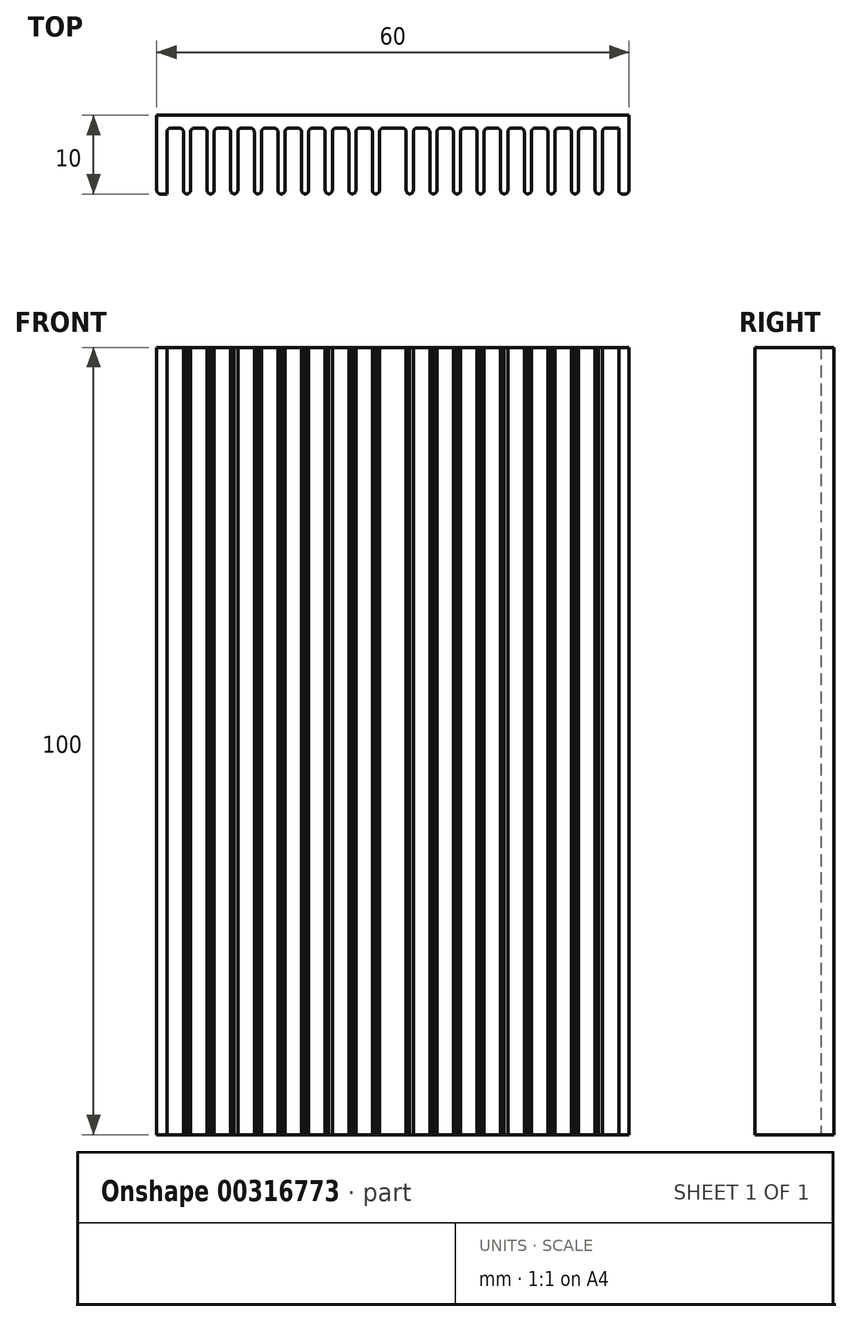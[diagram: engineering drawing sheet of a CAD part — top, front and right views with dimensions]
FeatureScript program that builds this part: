
annotation { "Feature Type Name" : "Feature", "Feature Type Description" : "" }
export const myFeature = defineFeature(function(context is Context, id is Id, definition is map)
    precondition{}
    {
        {
            var Q0;
            Q0=qCreatedBy(makeId("Front.planeOp"),FACE);
            var sketch = newSketch(context, id + "F0", { "sketchPlane" : qUnion([Q0])});
            skLineSegment(sketch, "E0.bottom", {"start": v(30, 50) * mm, "end": v(-30, 50) * mm});
            skLineSegment(sketch, "E0.top", {"start": v(30, -50) * mm, "end": v(-30, -50) * mm});
            skLineSegment(sketch, "E0.left", {"start": v(30, 50) * mm, "end": v(30, -50) * mm});
            skLineSegment(sketch, "E0.right", {"start": v(-30, 50) * mm, "end": v(-30, -50) * mm});
            skPoint(sketch, "E0.middle", {"position": v(0, 0) * mm});
            skSolve(sketch);
        }
        {
            var Q0;
            Q0=makeQuery(id+"F0.imprint","IMPRINT",FACE,{"disambiguationData":[TD([[makeQuery(id+"F0.imprint","IMPRINT",EDGE,{"derivedFrom":sQuery(id+"F0.wireOp",EDGE,"E0.bottom")}),1.0]])]});
            extrude(context, id + "F1", {"entities" : qUnion([Q0]), "depth" : 10 * mm});
        }
        {
            var Q0;
            Q0=makeQuery(id+"F1.opExtrude","SWEPT_FACE",FACE,{"disambiguationData":[OSD([sQuery(id+"F0.wireOp",EDGE,"E0.top")])]});
            var sketch = newSketch(context, id + "F2", { "sketchPlane" : qUnion([Q0])});
            skLineSegment(sketch, "E1.bottom", {"start": v(-28.7, 10) * mm, "end": v(-26.6, 10) * mm});
            skLineSegment(sketch, "E1.top", {"start": v(-28.7, 1.63) * mm, "end": v(-26.6, 1.63) * mm});
            skLineSegment(sketch, "E1.left", {"start": v(-28.7, 10) * mm, "end": v(-28.7, 1.63) * mm});
            skLineSegment(sketch, "E1.right", {"start": v(-26.6, 10) * mm, "end": v(-26.6, 1.63) * mm});
            skLineSegment(sketch, "E2.1.0.0", {"start": v(-25.7, 10) * mm, "end": v(-23.6, 10) * mm});
            skLineSegment(sketch, "E2.1.0.1", {"start": v(-25.7, 1.63) * mm, "end": v(-23.6, 1.63) * mm});
            skLineSegment(sketch, "E2.1.0.2", {"start": v(-25.7, 10) * mm, "end": v(-25.7, 1.63) * mm});
            skLineSegment(sketch, "E2.1.0.3", {"start": v(-23.6, 10) * mm, "end": v(-23.6, 1.63) * mm});
            skLineSegment(sketch, "E2.2.0.0", {"start": v(-22.7, 10) * mm, "end": v(-20.6, 10) * mm});
            skLineSegment(sketch, "E2.2.0.1", {"start": v(-22.7, 1.63) * mm, "end": v(-20.6, 1.63) * mm});
            skLineSegment(sketch, "E2.2.0.2", {"start": v(-22.7, 10) * mm, "end": v(-22.7, 1.63) * mm});
            skLineSegment(sketch, "E2.2.0.3", {"start": v(-20.6, 10) * mm, "end": v(-20.6, 1.63) * mm});
            skLineSegment(sketch, "E2.3.0.0", {"start": v(-19.7, 10) * mm, "end": v(-17.6, 10) * mm});
            skLineSegment(sketch, "E2.3.0.1", {"start": v(-19.7, 1.63) * mm, "end": v(-17.6, 1.63) * mm});
            skLineSegment(sketch, "E2.3.0.2", {"start": v(-19.7, 10) * mm, "end": v(-19.7, 1.63) * mm});
            skLineSegment(sketch, "E2.3.0.3", {"start": v(-17.6, 10) * mm, "end": v(-17.6, 1.63) * mm});
            skLineSegment(sketch, "E2.4.0.0", {"start": v(-16.7, 10) * mm, "end": v(-14.6, 10) * mm});
            skLineSegment(sketch, "E2.4.0.1", {"start": v(-16.7, 1.63) * mm, "end": v(-14.6, 1.63) * mm});
            skLineSegment(sketch, "E2.4.0.2", {"start": v(-16.7, 10) * mm, "end": v(-16.7, 1.63) * mm});
            skLineSegment(sketch, "E2.4.0.3", {"start": v(-14.6, 10) * mm, "end": v(-14.6, 1.63) * mm});
            skLineSegment(sketch, "E2.5.0.0", {"start": v(-13.7, 10) * mm, "end": v(-11.6, 10) * mm});
            skLineSegment(sketch, "E2.5.0.1", {"start": v(-13.7, 1.63) * mm, "end": v(-11.6, 1.63) * mm});
            skLineSegment(sketch, "E2.5.0.2", {"start": v(-13.7, 10) * mm, "end": v(-13.7, 1.63) * mm});
            skLineSegment(sketch, "E2.5.0.3", {"start": v(-11.6, 10) * mm, "end": v(-11.6, 1.63) * mm});
            skLineSegment(sketch, "E2.6.0.0", {"start": v(-10.7, 10) * mm, "end": v(-8.6, 10) * mm});
            skLineSegment(sketch, "E2.6.0.1", {"start": v(-10.7, 1.63) * mm, "end": v(-8.6, 1.63) * mm});
            skLineSegment(sketch, "E2.6.0.2", {"start": v(-10.7, 10) * mm, "end": v(-10.7, 1.63) * mm});
            skLineSegment(sketch, "E2.6.0.3", {"start": v(-8.6, 10) * mm, "end": v(-8.6, 1.63) * mm});
            skLineSegment(sketch, "E2.7.0.0", {"start": v(-7.7, 10) * mm, "end": v(-5.6, 10) * mm});
            skLineSegment(sketch, "E2.7.0.1", {"start": v(-7.7, 1.63) * mm, "end": v(-5.6, 1.63) * mm});
            skLineSegment(sketch, "E2.7.0.2", {"start": v(-7.7, 10) * mm, "end": v(-7.7, 1.63) * mm});
            skLineSegment(sketch, "E2.7.0.3", {"start": v(-5.6, 10) * mm, "end": v(-5.6, 1.63) * mm});
            skLineSegment(sketch, "E2.8.0.0", {"start": v(-4.7, 10) * mm, "end": v(-2.6, 10) * mm});
            skLineSegment(sketch, "E2.8.0.1", {"start": v(-4.7, 1.63) * mm, "end": v(-2.6, 1.63) * mm});
            skLineSegment(sketch, "E2.8.0.2", {"start": v(-4.7, 10) * mm, "end": v(-4.7, 1.63) * mm});
            skLineSegment(sketch, "E2.8.0.3", {"start": v(-2.6, 10) * mm, "end": v(-2.6, 1.63) * mm});
            skLineSegment(sketch, "E2.9.0.0", {"start": v(-1.7, 10) * mm, "end": v(0.4, 10) * mm});
            skLineSegment(sketch, "E2.9.0.1", {"start": v(-1.7, 1.63) * mm, "end": v(0.4, 1.63) * mm});
            skLineSegment(sketch, "E2.9.0.2", {"start": v(-1.7, 10) * mm, "end": v(-1.7, 1.63) * mm});
            skLineSegment(sketch, "E2.9.0.3", {"start": v(0.4, 10) * mm, "end": v(0.4, 1.63) * mm});
            skLineSegment(sketch, "E2.direction1", {"start": v(-28.7, 1.63) * mm, "end": v(-25.7, 1.63) * mm, "construction": true});
            skLineSegment(sketch, "E3.MirrorCS", {"start": v(25.7, 1.63) * mm, "end": v(23.6, 1.63) * mm});
            skLineSegment(sketch, "E4.MirrorCS", {"start": v(22.7, 1.63) * mm, "end": v(20.6, 1.63) * mm});
            skLineSegment(sketch, "E5.MirrorCS", {"start": v(19.7, 10) * mm, "end": v(17.6, 10) * mm});
            skLineSegment(sketch, "E6.MirrorCS", {"start": v(7.7, 1.63) * mm, "end": v(5.6, 1.63) * mm});
            skLineSegment(sketch, "E7.MirrorCS", {"start": v(19.7, 1.63) * mm, "end": v(17.6, 1.63) * mm});
            skLineSegment(sketch, "E8.MirrorCS", {"start": v(28.7, 1.63) * mm, "end": v(26.6, 1.63) * mm});
            skLineSegment(sketch, "E9.MirrorCS", {"start": v(10.7, 10) * mm, "end": v(8.6, 10) * mm});
            skLineSegment(sketch, "E10.MirrorCS", {"start": v(28.7, 1.63) * mm, "end": v(25.7, 1.63) * mm, "construction": true});
            skLineSegment(sketch, "E11.MirrorCS", {"start": v(4.7, 10) * mm, "end": v(2.6, 10) * mm});
            skLineSegment(sketch, "E12.MirrorCS", {"start": v(22.7, 10) * mm, "end": v(20.6, 10) * mm});
            skLineSegment(sketch, "E13.MirrorCS", {"start": v(10.7, 1.63) * mm, "end": v(8.6, 1.63) * mm});
            skLineSegment(sketch, "E14.MirrorCS", {"start": v(13.7, 10) * mm, "end": v(11.6, 10) * mm});
            skLineSegment(sketch, "E15.MirrorCS", {"start": v(1.7, 10) * mm, "end": v(-0.4, 10) * mm});
            skLineSegment(sketch, "E16.MirrorCS", {"start": v(16.7, 1.63) * mm, "end": v(14.6, 1.63) * mm});
            skLineSegment(sketch, "E17.MirrorCS", {"start": v(4.7, 1.63) * mm, "end": v(2.6, 1.63) * mm});
            skLineSegment(sketch, "E18.MirrorCS", {"start": v(16.7, 10) * mm, "end": v(14.6, 10) * mm});
            skLineSegment(sketch, "E19.MirrorCS", {"start": v(25.7, 10) * mm, "end": v(23.6, 10) * mm});
            skLineSegment(sketch, "E20.MirrorCS", {"start": v(7.7, 10) * mm, "end": v(5.6, 10) * mm});
            skLineSegment(sketch, "E21.MirrorCS", {"start": v(1.7, 1.63) * mm, "end": v(-0.4, 1.63) * mm});
            skLineSegment(sketch, "E22.MirrorCS", {"start": v(28.7, 10) * mm, "end": v(26.6, 10) * mm});
            skLineSegment(sketch, "E23.MirrorCS", {"start": v(13.7, 1.63) * mm, "end": v(11.6, 1.63) * mm});
            skLineSegment(sketch, "E24.MirrorCS", {"start": v(25.7, 10) * mm, "end": v(25.7, 1.63) * mm});
            skLineSegment(sketch, "E25.MirrorCS", {"start": v(23.6, 10) * mm, "end": v(23.6, 1.63) * mm});
            skLineSegment(sketch, "E26.MirrorCS", {"start": v(-0.4, 10) * mm, "end": v(-0.4, 1.63) * mm});
            skLineSegment(sketch, "E27.MirrorCS", {"start": v(13.7, 10) * mm, "end": v(13.7, 1.63) * mm});
            skLineSegment(sketch, "E28.MirrorCS", {"start": v(5.6, 10) * mm, "end": v(5.6, 1.63) * mm});
            skLineSegment(sketch, "E29.MirrorCS", {"start": v(22.7, 10) * mm, "end": v(22.7, 1.63) * mm});
            skLineSegment(sketch, "E30.MirrorCS", {"start": v(20.6, 10) * mm, "end": v(20.6, 1.63) * mm});
            skLineSegment(sketch, "E31.MirrorCS", {"start": v(7.7, 10) * mm, "end": v(7.7, 1.63) * mm});
            skLineSegment(sketch, "E32.MirrorCS", {"start": v(4.7, 10) * mm, "end": v(4.7, 1.63) * mm});
            skLineSegment(sketch, "E33.MirrorCS", {"start": v(16.7, 10) * mm, "end": v(16.7, 1.63) * mm});
            skLineSegment(sketch, "E34.MirrorCS", {"start": v(10.7, 10) * mm, "end": v(10.7, 1.63) * mm});
            skLineSegment(sketch, "E35.MirrorCS", {"start": v(8.6, 10) * mm, "end": v(8.6, 1.63) * mm});
            skLineSegment(sketch, "E36.MirrorCS", {"start": v(19.7, 10) * mm, "end": v(19.7, 1.63) * mm});
            skLineSegment(sketch, "E37.MirrorCS", {"start": v(26.6, 10) * mm, "end": v(26.6, 1.63) * mm});
            skLineSegment(sketch, "E38.MirrorCS", {"start": v(28.7, 10) * mm, "end": v(28.7, 1.63) * mm});
            skLineSegment(sketch, "E39.MirrorCS", {"start": v(1.7, 10) * mm, "end": v(1.7, 1.63) * mm});
            skLineSegment(sketch, "E40.MirrorCS", {"start": v(2.6, 10) * mm, "end": v(2.6, 1.63) * mm});
            skLineSegment(sketch, "E41.MirrorCS", {"start": v(17.6, 10) * mm, "end": v(17.6, 1.63) * mm});
            skLineSegment(sketch, "E42.MirrorCS", {"start": v(11.6, 10) * mm, "end": v(11.6, 1.63) * mm});
            skLineSegment(sketch, "E43.MirrorCS", {"start": v(14.6, 10) * mm, "end": v(14.6, 1.63) * mm});
            skSolve(sketch);
        }
        {
            var Q0;
            Q0=makeQuery(id+"F2.imprint","IMPRINT",FACE,{"disambiguationData":[TD([[makeQuery(id+"F2.imprint","IMPRINT",EDGE,{"derivedFrom":sQuery(id+"F2.wireOp",EDGE,"E2.1.0.0")}),1.0]])]});
            var Q1;
            Q1=makeQuery(id+"F2.imprint","IMPRINT",FACE,{"disambiguationData":[TD([[makeQuery(id+"F2.imprint","IMPRINT",EDGE,{"derivedFrom":sQuery(id+"F2.wireOp",EDGE,"E2.2.0.0")}),1.0]])]});
            var Q2;
            Q2=makeQuery(id+"F2.imprint","IMPRINT",FACE,{"disambiguationData":[TD([[makeQuery(id+"F2.imprint","IMPRINT",EDGE,{"derivedFrom":sQuery(id+"F2.wireOp",EDGE,"E2.3.0.0")}),1.0]])]});
            var Q3;
            Q3=makeQuery(id+"F2.imprint","IMPRINT",FACE,{"disambiguationData":[TD([[makeQuery(id+"F2.imprint","IMPRINT",EDGE,{"derivedFrom":sQuery(id+"F2.wireOp",EDGE,"E2.4.0.0")}),1.0]])]});
            var Q4;
            Q4=makeQuery(id+"F2.imprint","IMPRINT",FACE,{"disambiguationData":[TD([[makeQuery(id+"F2.imprint","IMPRINT",EDGE,{"derivedFrom":sQuery(id+"F2.wireOp",EDGE,"E2.5.0.0")}),1.0]])]});
            var Q5;
            Q5=makeQuery(id+"F2.imprint","IMPRINT",FACE,{"disambiguationData":[TD([[makeQuery(id+"F2.imprint","IMPRINT",EDGE,{"derivedFrom":sQuery(id+"F2.wireOp",EDGE,"E2.6.0.0")}),1.0]])]});
            var Q6;
            Q6=makeQuery(id+"F2.imprint","IMPRINT",FACE,{"disambiguationData":[TD([[makeQuery(id+"F2.imprint","IMPRINT",EDGE,{"derivedFrom":sQuery(id+"F2.wireOp",EDGE,"E2.7.0.0")}),1.0]])]});
            var Q7;
            Q7=makeQuery(id+"F2.imprint","IMPRINT",FACE,{"disambiguationData":[TD([[makeQuery(id+"F2.imprint","IMPRINT",EDGE,{"derivedFrom":sQuery(id+"F2.wireOp",EDGE,"E2.8.0.0")}),1.0]])]});
            var Q8;
            Q8=makeQuery(id+"F2.imprint","IMPRINT",FACE,{"disambiguationData":[TD([[makeQuery(id+"F2.imprint","IMPRINT",EDGE,{"derivedFrom":sQuery(id+"F2.wireOp",EDGE,"E2.9.0.0")}),1.0]])]});
            var Q9;
            Q9=makeQuery(id+"F2.imprint","IMPRINT",FACE,{"disambiguationData":[TD([[makeQuery(id+"F2.imprint","IMPRINT",EDGE,{"derivedFrom":sQuery(id+"F2.wireOp",EDGE,"E3.MirrorCS")}),-1.0]])]});
            var Q10;
            Q10=makeQuery(id+"F2.imprint","IMPRINT",FACE,{"disambiguationData":[TD([[makeQuery(id+"F2.imprint","IMPRINT",EDGE,{"derivedFrom":sQuery(id+"F2.wireOp",EDGE,"E4.MirrorCS")}),-1.0]])]});
            var Q11;
            Q11=makeQuery(id+"F2.imprint","IMPRINT",FACE,{"disambiguationData":[TD([[makeQuery(id+"F2.imprint","IMPRINT",EDGE,{"derivedFrom":sQuery(id+"F2.wireOp",EDGE,"E5.MirrorCS")}),1.0]])]});
            var Q12;
            Q12=makeQuery(id+"F2.imprint","IMPRINT",FACE,{"disambiguationData":[TD([[makeQuery(id+"F2.imprint","IMPRINT",EDGE,{"derivedFrom":sQuery(id+"F2.wireOp",EDGE,"E6.MirrorCS")}),-1.0]])]});
            var Q13;
            Q13=makeQuery(id+"F2.imprint","IMPRINT",FACE,{"disambiguationData":[TD([[makeQuery(id+"F2.imprint","IMPRINT",EDGE,{"derivedFrom":sQuery(id+"F2.wireOp",EDGE,"E8.MirrorCS")}),-1.0]])]});
            var Q14;
            Q14=makeQuery(id+"F2.imprint","IMPRINT",FACE,{"disambiguationData":[TD([[makeQuery(id+"F2.imprint","IMPRINT",EDGE,{"derivedFrom":sQuery(id+"F2.wireOp",EDGE,"E9.MirrorCS")}),1.0]])]});
            var Q15;
            Q15=makeQuery(id+"F2.imprint","IMPRINT",FACE,{"disambiguationData":[TD([[makeQuery(id+"F2.imprint","IMPRINT",EDGE,{"derivedFrom":sQuery(id+"F2.wireOp",EDGE,"E11.MirrorCS")}),1.0]])]});
            var Q16;
            Q16=makeQuery(id+"F2.imprint","IMPRINT",FACE,{"disambiguationData":[TD([[makeQuery(id+"F2.imprint","IMPRINT",EDGE,{"derivedFrom":sQuery(id+"F2.wireOp",EDGE,"E14.MirrorCS")}),1.0]])]});
            var Q17;
            Q17=makeQuery(id+"F2.imprint","IMPRINT",FACE,{"disambiguationData":[TD([[makeQuery(id+"F2.imprint","IMPRINT",EDGE,{"derivedFrom":sQuery(id+"F2.wireOp",EDGE,"E15.MirrorCS")}),1.0]])]});
            var Q18;
            Q18=makeQuery(id+"F2.imprint","IMPRINT",FACE,{"disambiguationData":[TD([[makeQuery(id+"F2.imprint","IMPRINT",EDGE,{"derivedFrom":sQuery(id+"F2.wireOp",EDGE,"E16.MirrorCS")}),-1.0]])]});
            var Q19;
            Q19=makeQuery(id+"F2.imprint","IMPRINT",FACE,{"disambiguationData":[TD([[makeQuery(id+"F2.imprint","IMPRINT",EDGE,{"derivedFrom":sQuery(id+"F2.wireOp",EDGE,"E1.bottom")}),1.0]])]});
            extrude(context, id + "F3", {"entities" : qUnion([Q0, Q1, Q2, Q3, Q4, Q5, Q6, Q7, Q8, Q9, Q10, Q11, Q12, Q13, Q14, Q15, Q16, Q17, Q18, Q19]), "operationType" : NewBodyOperationType.REMOVE, "endBound" : BoundingType.THROUGH_ALL, "oppositeDirection" : true, "depth" : 25 * mm});
        }
        {
            var Q0;
            Q0=makeQuery(id+"F3.boolean.opBoolean","COPY",EDGE,{"derivedFrom":makeQuery(id+"F3.opExtrude","SWEPT_EDGE",EDGE,{"disambiguationData":[OSD([sQuery(id+"F0.wireOp",EDGE,"E0.top"),sQuery(id+"F2.wireOp",EDGE,"E1.bottom"),sQuery(id+"F2.wireOp",EDGE,"E1.left")])]})});
            var Q1;
            Q1=makeQuery(id+"F3.boolean.opBoolean","COPY",EDGE,{"derivedFrom":makeQuery(id+"F3.opExtrude","SWEPT_EDGE",EDGE,{"disambiguationData":[OSD([sQuery(id+"F2.wireOp",EDGE,"E1.top"),sQuery(id+"F2.wireOp",EDGE,"E1.left")])]})});
            var Q2;
            Q2=makeQuery(id+"F3.boolean.opBoolean","COPY",EDGE,{"derivedFrom":makeQuery(id+"F3.opExtrude","SWEPT_EDGE",EDGE,{"disambiguationData":[OSD([sQuery(id+"F2.wireOp",EDGE,"E1.top"),sQuery(id+"F2.wireOp",EDGE,"E1.right")])]})});
            var Q3;
            Q3=makeQuery(id+"F3.boolean.opBoolean","COPY",EDGE,{"derivedFrom":makeQuery(id+"F3.opExtrude","SWEPT_EDGE",EDGE,{"disambiguationData":[OSD([sQuery(id+"F0.wireOp",EDGE,"E0.top"),sQuery(id+"F2.wireOp",EDGE,"E1.bottom"),sQuery(id+"F2.wireOp",EDGE,"E1.right")])]})});
            var Q4;
            Q4=makeQuery(id+"F3.boolean.opBoolean","COPY",EDGE,{"derivedFrom":makeQuery(id+"F3.opExtrude","SWEPT_EDGE",EDGE,{"disambiguationData":[OSD([sQuery(id+"F0.wireOp",EDGE,"E0.top"),sQuery(id+"F2.wireOp",EDGE,"E2.1.0.0"),sQuery(id+"F2.wireOp",EDGE,"E2.1.0.2")])]})});
            var Q5;
            Q5=makeQuery(id+"F3.boolean.opBoolean","COPY",EDGE,{"derivedFrom":makeQuery(id+"F3.opExtrude","SWEPT_EDGE",EDGE,{"disambiguationData":[OSD([sQuery(id+"F2.wireOp",EDGE,"E2.1.0.1"),sQuery(id+"F2.wireOp",EDGE,"E2.1.0.2")])]})});
            var Q6;
            Q6=makeQuery(id+"F3.boolean.opBoolean","COPY",EDGE,{"derivedFrom":makeQuery(id+"F3.opExtrude","SWEPT_EDGE",EDGE,{"disambiguationData":[OSD([sQuery(id+"F2.wireOp",EDGE,"E2.2.0.1"),sQuery(id+"F2.wireOp",EDGE,"E2.2.0.2")])]})});
            var Q7;
            Q7=makeQuery(id+"F3.boolean.opBoolean","COPY",EDGE,{"derivedFrom":makeQuery(id+"F3.opExtrude","SWEPT_EDGE",EDGE,{"disambiguationData":[OSD([sQuery(id+"F2.wireOp",EDGE,"E2.3.0.1"),sQuery(id+"F2.wireOp",EDGE,"E2.3.0.2")])]})});
            var Q8;
            Q8=makeQuery(id+"F3.boolean.opBoolean","COPY",EDGE,{"derivedFrom":makeQuery(id+"F3.opExtrude","SWEPT_EDGE",EDGE,{"disambiguationData":[OSD([sQuery(id+"F2.wireOp",EDGE,"E2.4.0.1"),sQuery(id+"F2.wireOp",EDGE,"E2.4.0.2")])]})});
            var Q9;
            Q9=makeQuery(id+"F3.boolean.opBoolean","COPY",EDGE,{"derivedFrom":makeQuery(id+"F3.opExtrude","SWEPT_EDGE",EDGE,{"disambiguationData":[OSD([sQuery(id+"F2.wireOp",EDGE,"E2.5.0.1"),sQuery(id+"F2.wireOp",EDGE,"E2.5.0.2")])]})});
            var Q10;
            Q10=makeQuery(id+"F3.boolean.opBoolean","COPY",EDGE,{"derivedFrom":makeQuery(id+"F3.opExtrude","SWEPT_EDGE",EDGE,{"disambiguationData":[OSD([sQuery(id+"F2.wireOp",EDGE,"E2.6.0.1"),sQuery(id+"F2.wireOp",EDGE,"E2.6.0.2")])]})});
            var Q11;
            Q11=makeQuery(id+"F3.boolean.opBoolean","COPY",EDGE,{"derivedFrom":makeQuery(id+"F3.opExtrude","SWEPT_EDGE",EDGE,{"disambiguationData":[OSD([sQuery(id+"F2.wireOp",EDGE,"E2.7.0.1"),sQuery(id+"F2.wireOp",EDGE,"E2.7.0.2")])]})});
            var Q12;
            Q12=makeQuery(id+"F3.boolean.opBoolean","COPY",EDGE,{"derivedFrom":makeQuery(id+"F3.opExtrude","SWEPT_EDGE",EDGE,{"disambiguationData":[OSD([sQuery(id+"F2.wireOp",EDGE,"E2.8.0.1"),sQuery(id+"F2.wireOp",EDGE,"E2.8.0.2")])]})});
            var Q13;
            Q13=makeQuery(id+"F3.boolean.opBoolean","COPY",EDGE,{"derivedFrom":makeQuery(id+"F3.opExtrude","SWEPT_EDGE",EDGE,{"disambiguationData":[OSD([sQuery(id+"F2.wireOp",EDGE,"E2.9.0.1"),sQuery(id+"F2.wireOp",EDGE,"E2.9.0.2")])]})});
            var Q14;
            Q14=makeQuery(id+"F3.boolean.opBoolean","COPY",EDGE,{"derivedFrom":makeQuery(id+"F3.opExtrude","SWEPT_EDGE",EDGE,{"disambiguationData":[OSD([sQuery(id+"F2.wireOp",EDGE,"E17.MirrorCS"),sQuery(id+"F2.wireOp",EDGE,"E40.MirrorCS")])]})});
            var Q15;
            Q15=makeQuery(id+"F3.boolean.opBoolean","COPY",EDGE,{"derivedFrom":makeQuery(id+"F3.opExtrude","SWEPT_EDGE",EDGE,{"disambiguationData":[OSD([sQuery(id+"F2.wireOp",EDGE,"E6.MirrorCS"),sQuery(id+"F2.wireOp",EDGE,"E28.MirrorCS")])]})});
            var Q16;
            Q16=makeQuery(id+"F3.boolean.opBoolean","COPY",EDGE,{"derivedFrom":makeQuery(id+"F3.opExtrude","SWEPT_EDGE",EDGE,{"disambiguationData":[OSD([sQuery(id+"F2.wireOp",EDGE,"E13.MirrorCS"),sQuery(id+"F2.wireOp",EDGE,"E35.MirrorCS")])]})});
            var Q17;
            Q17=makeQuery(id+"F3.boolean.opBoolean","COPY",EDGE,{"derivedFrom":makeQuery(id+"F3.opExtrude","SWEPT_EDGE",EDGE,{"disambiguationData":[OSD([sQuery(id+"F2.wireOp",EDGE,"E23.MirrorCS"),sQuery(id+"F2.wireOp",EDGE,"E42.MirrorCS")])]})});
            var Q18;
            Q18=makeQuery(id+"F3.boolean.opBoolean","COPY",EDGE,{"derivedFrom":makeQuery(id+"F3.opExtrude","SWEPT_EDGE",EDGE,{"disambiguationData":[OSD([sQuery(id+"F2.wireOp",EDGE,"E16.MirrorCS"),sQuery(id+"F2.wireOp",EDGE,"E43.MirrorCS")])]})});
            var Q19;
            Q19=makeQuery(id+"F3.boolean.opBoolean","COPY",EDGE,{"derivedFrom":makeQuery(id+"F3.opExtrude","SWEPT_EDGE",EDGE,{"disambiguationData":[OSD([sQuery(id+"F2.wireOp",EDGE,"E7.MirrorCS"),sQuery(id+"F2.wireOp",EDGE,"E41.MirrorCS")])]})});
            var Q20;
            Q20=makeQuery(id+"F3.boolean.opBoolean","COPY",EDGE,{"derivedFrom":makeQuery(id+"F3.opExtrude","SWEPT_EDGE",EDGE,{"disambiguationData":[OSD([sQuery(id+"F2.wireOp",EDGE,"E4.MirrorCS"),sQuery(id+"F2.wireOp",EDGE,"E30.MirrorCS")])]})});
            var Q21;
            Q21=makeQuery(id+"F3.boolean.opBoolean","COPY",EDGE,{"derivedFrom":makeQuery(id+"F3.opExtrude","SWEPT_EDGE",EDGE,{"disambiguationData":[OSD([sQuery(id+"F2.wireOp",EDGE,"E3.MirrorCS"),sQuery(id+"F2.wireOp",EDGE,"E25.MirrorCS")])]})});
            var Q22;
            Q22=makeQuery(id+"F3.boolean.opBoolean","COPY",EDGE,{"derivedFrom":makeQuery(id+"F3.opExtrude","SWEPT_EDGE",EDGE,{"disambiguationData":[OSD([sQuery(id+"F2.wireOp",EDGE,"E8.MirrorCS"),sQuery(id+"F2.wireOp",EDGE,"E37.MirrorCS")])]})});
            var Q23;
            Q23=makeQuery(id+"F3.boolean.opBoolean","COPY",EDGE,{"derivedFrom":makeQuery(id+"F3.opExtrude","SWEPT_EDGE",EDGE,{"disambiguationData":[OSD([sQuery(id+"F0.wireOp",EDGE,"E0.top"),sQuery(id+"F2.wireOp",EDGE,"E2.2.0.0"),sQuery(id+"F2.wireOp",EDGE,"E2.2.0.2")])]})});
            var Q24;
            Q24=makeQuery(id+"F3.boolean.opBoolean","COPY",EDGE,{"derivedFrom":makeQuery(id+"F3.opExtrude","SWEPT_EDGE",EDGE,{"disambiguationData":[OSD([sQuery(id+"F0.wireOp",EDGE,"E0.top"),sQuery(id+"F2.wireOp",EDGE,"E2.3.0.0"),sQuery(id+"F2.wireOp",EDGE,"E2.3.0.2")])]})});
            var Q25;
            Q25=makeQuery(id+"F3.boolean.opBoolean","COPY",EDGE,{"derivedFrom":makeQuery(id+"F3.opExtrude","SWEPT_EDGE",EDGE,{"disambiguationData":[OSD([sQuery(id+"F0.wireOp",EDGE,"E0.top"),sQuery(id+"F2.wireOp",EDGE,"E2.4.0.0"),sQuery(id+"F2.wireOp",EDGE,"E2.4.0.2")])]})});
            var Q26;
            Q26=makeQuery(id+"F3.boolean.opBoolean","COPY",EDGE,{"derivedFrom":makeQuery(id+"F3.opExtrude","SWEPT_EDGE",EDGE,{"disambiguationData":[OSD([sQuery(id+"F0.wireOp",EDGE,"E0.top"),sQuery(id+"F2.wireOp",EDGE,"E2.5.0.0"),sQuery(id+"F2.wireOp",EDGE,"E2.5.0.2")])]})});
            var Q27;
            Q27=makeQuery(id+"F3.boolean.opBoolean","COPY",EDGE,{"derivedFrom":makeQuery(id+"F3.opExtrude","SWEPT_EDGE",EDGE,{"disambiguationData":[OSD([sQuery(id+"F0.wireOp",EDGE,"E0.top"),sQuery(id+"F2.wireOp",EDGE,"E2.6.0.0"),sQuery(id+"F2.wireOp",EDGE,"E2.6.0.2")])]})});
            var Q28;
            Q28=makeQuery(id+"F3.boolean.opBoolean","COPY",EDGE,{"derivedFrom":makeQuery(id+"F3.opExtrude","SWEPT_EDGE",EDGE,{"disambiguationData":[OSD([sQuery(id+"F0.wireOp",EDGE,"E0.top"),sQuery(id+"F2.wireOp",EDGE,"E2.7.0.0"),sQuery(id+"F2.wireOp",EDGE,"E2.7.0.2")])]})});
            var Q29;
            Q29=makeQuery(id+"F3.boolean.opBoolean","COPY",EDGE,{"derivedFrom":makeQuery(id+"F3.opExtrude","SWEPT_EDGE",EDGE,{"disambiguationData":[OSD([sQuery(id+"F0.wireOp",EDGE,"E0.top"),sQuery(id+"F2.wireOp",EDGE,"E2.8.0.0"),sQuery(id+"F2.wireOp",EDGE,"E2.8.0.2")])]})});
            var Q30;
            Q30=makeQuery(id+"F3.boolean.opBoolean","COPY",EDGE,{"derivedFrom":makeQuery(id+"F3.opExtrude","SWEPT_EDGE",EDGE,{"disambiguationData":[OSD([sQuery(id+"F0.wireOp",EDGE,"E0.top"),sQuery(id+"F2.wireOp",EDGE,"E2.9.0.0"),sQuery(id+"F2.wireOp",EDGE,"E2.9.0.2")])]})});
            var Q31;
            Q31=makeQuery(id+"F3.boolean.opBoolean","COPY",EDGE,{"derivedFrom":makeQuery(id+"F3.opExtrude","SWEPT_EDGE",EDGE,{"disambiguationData":[OSD([sQuery(id+"F0.wireOp",EDGE,"E0.top"),sQuery(id+"F2.wireOp",EDGE,"E11.MirrorCS"),sQuery(id+"F2.wireOp",EDGE,"E40.MirrorCS")])]})});
            var Q32;
            Q32=makeQuery(id+"F3.boolean.opBoolean","COPY",EDGE,{"derivedFrom":makeQuery(id+"F3.opExtrude","SWEPT_EDGE",EDGE,{"disambiguationData":[OSD([sQuery(id+"F0.wireOp",EDGE,"E0.top"),sQuery(id+"F2.wireOp",EDGE,"E20.MirrorCS"),sQuery(id+"F2.wireOp",EDGE,"E28.MirrorCS")])]})});
            var Q33;
            Q33=makeQuery(id+"F3.boolean.opBoolean","COPY",EDGE,{"derivedFrom":makeQuery(id+"F3.opExtrude","SWEPT_EDGE",EDGE,{"disambiguationData":[OSD([sQuery(id+"F0.wireOp",EDGE,"E0.top"),sQuery(id+"F2.wireOp",EDGE,"E9.MirrorCS"),sQuery(id+"F2.wireOp",EDGE,"E35.MirrorCS")])]})});
            var Q34;
            Q34=makeQuery(id+"F3.boolean.opBoolean","COPY",EDGE,{"derivedFrom":makeQuery(id+"F3.opExtrude","SWEPT_EDGE",EDGE,{"disambiguationData":[OSD([sQuery(id+"F0.wireOp",EDGE,"E0.top"),sQuery(id+"F2.wireOp",EDGE,"E14.MirrorCS"),sQuery(id+"F2.wireOp",EDGE,"E42.MirrorCS")])]})});
            var Q35;
            Q35=makeQuery(id+"F3.boolean.opBoolean","COPY",EDGE,{"derivedFrom":makeQuery(id+"F3.opExtrude","SWEPT_EDGE",EDGE,{"disambiguationData":[OSD([sQuery(id+"F0.wireOp",EDGE,"E0.top"),sQuery(id+"F2.wireOp",EDGE,"E18.MirrorCS"),sQuery(id+"F2.wireOp",EDGE,"E43.MirrorCS")])]})});
            var Q36;
            Q36=makeQuery(id+"F3.boolean.opBoolean","COPY",EDGE,{"derivedFrom":makeQuery(id+"F3.opExtrude","SWEPT_EDGE",EDGE,{"disambiguationData":[OSD([sQuery(id+"F0.wireOp",EDGE,"E0.top"),sQuery(id+"F2.wireOp",EDGE,"E5.MirrorCS"),sQuery(id+"F2.wireOp",EDGE,"E41.MirrorCS")])]})});
            var Q37;
            Q37=makeQuery(id+"F3.boolean.opBoolean","COPY",EDGE,{"derivedFrom":makeQuery(id+"F3.opExtrude","SWEPT_EDGE",EDGE,{"disambiguationData":[OSD([sQuery(id+"F0.wireOp",EDGE,"E0.top"),sQuery(id+"F2.wireOp",EDGE,"E12.MirrorCS"),sQuery(id+"F2.wireOp",EDGE,"E30.MirrorCS")])]})});
            var Q38;
            Q38=makeQuery(id+"F3.boolean.opBoolean","COPY",EDGE,{"derivedFrom":makeQuery(id+"F3.opExtrude","SWEPT_EDGE",EDGE,{"disambiguationData":[OSD([sQuery(id+"F0.wireOp",EDGE,"E0.top"),sQuery(id+"F2.wireOp",EDGE,"E19.MirrorCS"),sQuery(id+"F2.wireOp",EDGE,"E25.MirrorCS")])]})});
            var Q39;
            Q39=makeQuery(id+"F3.boolean.opBoolean","COPY",EDGE,{"derivedFrom":makeQuery(id+"F3.opExtrude","SWEPT_EDGE",EDGE,{"disambiguationData":[OSD([sQuery(id+"F0.wireOp",EDGE,"E0.top"),sQuery(id+"F2.wireOp",EDGE,"E22.MirrorCS"),sQuery(id+"F2.wireOp",EDGE,"E37.MirrorCS")])]})});
            var Q40;
            Q40=makeQuery(id+"F3.boolean.opBoolean","COPY",EDGE,{"derivedFrom":makeQuery(id+"F3.opExtrude","SWEPT_EDGE",EDGE,{"disambiguationData":[OSD([sQuery(id+"F0.wireOp",EDGE,"E0.top"),sQuery(id+"F2.wireOp",EDGE,"E22.MirrorCS"),sQuery(id+"F2.wireOp",EDGE,"E38.MirrorCS")])]})});
            var Q41;
            Q41=makeQuery(id+"F1.opExtrude","CAP_EDGE",EDGE,{"disambiguationData":[OSD([sQuery(id+"F0.wireOp",EDGE,"E0.left")])],"isStart":false});
            var Q42;
            Q42=makeQuery(id+"F1.opExtrude","CAP_EDGE",EDGE,{"disambiguationData":[OSD([sQuery(id+"F0.wireOp",EDGE,"E0.right")])],"isStart":false});
            var Q43;
            Q43=makeQuery(id+"F3.boolean.opBoolean","COPY",EDGE,{"derivedFrom":makeQuery(id+"F3.opExtrude","SWEPT_EDGE",EDGE,{"disambiguationData":[OSD([sQuery(id+"F2.wireOp",EDGE,"E2.1.0.1"),sQuery(id+"F2.wireOp",EDGE,"E2.1.0.3")])]})});
            var Q44;
            Q44=makeQuery(id+"F3.boolean.opBoolean","COPY",EDGE,{"derivedFrom":makeQuery(id+"F3.opExtrude","SWEPT_EDGE",EDGE,{"disambiguationData":[OSD([sQuery(id+"F2.wireOp",EDGE,"E2.2.0.1"),sQuery(id+"F2.wireOp",EDGE,"E2.2.0.3")])]})});
            var Q45;
            Q45=makeQuery(id+"F3.boolean.opBoolean","COPY",EDGE,{"derivedFrom":makeQuery(id+"F3.opExtrude","SWEPT_EDGE",EDGE,{"disambiguationData":[OSD([sQuery(id+"F2.wireOp",EDGE,"E2.3.0.1"),sQuery(id+"F2.wireOp",EDGE,"E2.3.0.3")])]})});
            var Q46;
            Q46=makeQuery(id+"F3.boolean.opBoolean","COPY",EDGE,{"derivedFrom":makeQuery(id+"F3.opExtrude","SWEPT_EDGE",EDGE,{"disambiguationData":[OSD([sQuery(id+"F2.wireOp",EDGE,"E2.4.0.1"),sQuery(id+"F2.wireOp",EDGE,"E2.4.0.3")])]})});
            var Q47;
            Q47=makeQuery(id+"F3.boolean.opBoolean","COPY",EDGE,{"derivedFrom":makeQuery(id+"F3.opExtrude","SWEPT_EDGE",EDGE,{"disambiguationData":[OSD([sQuery(id+"F2.wireOp",EDGE,"E2.5.0.1"),sQuery(id+"F2.wireOp",EDGE,"E2.5.0.3")])]})});
            var Q48;
            Q48=makeQuery(id+"F3.boolean.opBoolean","COPY",EDGE,{"derivedFrom":makeQuery(id+"F3.opExtrude","SWEPT_EDGE",EDGE,{"disambiguationData":[OSD([sQuery(id+"F2.wireOp",EDGE,"E2.6.0.1"),sQuery(id+"F2.wireOp",EDGE,"E2.6.0.3")])]})});
            var Q49;
            Q49=makeQuery(id+"F3.boolean.opBoolean","COPY",EDGE,{"derivedFrom":makeQuery(id+"F3.opExtrude","SWEPT_EDGE",EDGE,{"disambiguationData":[OSD([sQuery(id+"F2.wireOp",EDGE,"E2.7.0.1"),sQuery(id+"F2.wireOp",EDGE,"E2.7.0.3")])]})});
            var Q50;
            Q50=makeQuery(id+"F3.boolean.opBoolean","COPY",EDGE,{"derivedFrom":makeQuery(id+"F3.opExtrude","SWEPT_EDGE",EDGE,{"disambiguationData":[OSD([sQuery(id+"F2.wireOp",EDGE,"E2.8.0.1"),sQuery(id+"F2.wireOp",EDGE,"E2.8.0.3")])]})});
            var Q51;
            Q51=makeQuery(id+"F3.boolean.opBoolean","COPY",EDGE,{"derivedFrom":makeQuery(id+"F3.opExtrude","SWEPT_EDGE",EDGE,{"disambiguationData":[OSD([sQuery(id+"F2.wireOp",EDGE,"E21.MirrorCS"),sQuery(id+"F2.wireOp",EDGE,"E39.MirrorCS")])]})});
            var Q52;
            Q52=makeQuery(id+"F3.boolean.opBoolean","COPY",EDGE,{"derivedFrom":makeQuery(id+"F3.opExtrude","SWEPT_EDGE",EDGE,{"disambiguationData":[OSD([sQuery(id+"F2.wireOp",EDGE,"E17.MirrorCS"),sQuery(id+"F2.wireOp",EDGE,"E32.MirrorCS")])]})});
            var Q53;
            Q53=makeQuery(id+"F3.boolean.opBoolean","COPY",EDGE,{"derivedFrom":makeQuery(id+"F3.opExtrude","SWEPT_EDGE",EDGE,{"disambiguationData":[OSD([sQuery(id+"F2.wireOp",EDGE,"E6.MirrorCS"),sQuery(id+"F2.wireOp",EDGE,"E31.MirrorCS")])]})});
            var Q54;
            Q54=makeQuery(id+"F3.boolean.opBoolean","COPY",EDGE,{"derivedFrom":makeQuery(id+"F3.opExtrude","SWEPT_EDGE",EDGE,{"disambiguationData":[OSD([sQuery(id+"F2.wireOp",EDGE,"E13.MirrorCS"),sQuery(id+"F2.wireOp",EDGE,"E34.MirrorCS")])]})});
            var Q55;
            Q55=makeQuery(id+"F3.boolean.opBoolean","COPY",EDGE,{"derivedFrom":makeQuery(id+"F3.opExtrude","SWEPT_EDGE",EDGE,{"disambiguationData":[OSD([sQuery(id+"F2.wireOp",EDGE,"E23.MirrorCS"),sQuery(id+"F2.wireOp",EDGE,"E27.MirrorCS")])]})});
            var Q56;
            Q56=makeQuery(id+"F3.boolean.opBoolean","COPY",EDGE,{"derivedFrom":makeQuery(id+"F3.opExtrude","SWEPT_EDGE",EDGE,{"disambiguationData":[OSD([sQuery(id+"F2.wireOp",EDGE,"E16.MirrorCS"),sQuery(id+"F2.wireOp",EDGE,"E33.MirrorCS")])]})});
            var Q57;
            Q57=makeQuery(id+"F3.boolean.opBoolean","COPY",EDGE,{"derivedFrom":makeQuery(id+"F3.opExtrude","SWEPT_EDGE",EDGE,{"disambiguationData":[OSD([sQuery(id+"F2.wireOp",EDGE,"E7.MirrorCS"),sQuery(id+"F2.wireOp",EDGE,"E36.MirrorCS")])]})});
            var Q58;
            Q58=makeQuery(id+"F3.boolean.opBoolean","COPY",EDGE,{"derivedFrom":makeQuery(id+"F3.opExtrude","SWEPT_EDGE",EDGE,{"disambiguationData":[OSD([sQuery(id+"F2.wireOp",EDGE,"E4.MirrorCS"),sQuery(id+"F2.wireOp",EDGE,"E29.MirrorCS")])]})});
            var Q59;
            Q59=makeQuery(id+"F3.boolean.opBoolean","COPY",EDGE,{"derivedFrom":makeQuery(id+"F3.opExtrude","SWEPT_EDGE",EDGE,{"disambiguationData":[OSD([sQuery(id+"F2.wireOp",EDGE,"E3.MirrorCS"),sQuery(id+"F2.wireOp",EDGE,"E24.MirrorCS")])]})});
            var Q60;
            Q60=makeQuery(id+"F3.boolean.opBoolean","COPY",EDGE,{"derivedFrom":makeQuery(id+"F3.opExtrude","SWEPT_EDGE",EDGE,{"disambiguationData":[OSD([sQuery(id+"F0.wireOp",EDGE,"E0.top"),sQuery(id+"F2.wireOp",EDGE,"E2.1.0.0"),sQuery(id+"F2.wireOp",EDGE,"E2.1.0.3")])]})});
            var Q61;
            Q61=makeQuery(id+"F3.boolean.opBoolean","COPY",EDGE,{"derivedFrom":makeQuery(id+"F3.opExtrude","SWEPT_EDGE",EDGE,{"disambiguationData":[OSD([sQuery(id+"F0.wireOp",EDGE,"E0.top"),sQuery(id+"F2.wireOp",EDGE,"E2.2.0.0"),sQuery(id+"F2.wireOp",EDGE,"E2.2.0.3")])]})});
            var Q62;
            Q62=makeQuery(id+"F3.boolean.opBoolean","COPY",EDGE,{"derivedFrom":makeQuery(id+"F3.opExtrude","SWEPT_EDGE",EDGE,{"disambiguationData":[OSD([sQuery(id+"F0.wireOp",EDGE,"E0.top"),sQuery(id+"F2.wireOp",EDGE,"E2.3.0.0"),sQuery(id+"F2.wireOp",EDGE,"E2.3.0.3")])]})});
            var Q63;
            Q63=makeQuery(id+"F3.boolean.opBoolean","COPY",EDGE,{"derivedFrom":makeQuery(id+"F3.opExtrude","SWEPT_EDGE",EDGE,{"disambiguationData":[OSD([sQuery(id+"F0.wireOp",EDGE,"E0.top"),sQuery(id+"F2.wireOp",EDGE,"E2.4.0.0"),sQuery(id+"F2.wireOp",EDGE,"E2.4.0.3")])]})});
            var Q64;
            Q64=makeQuery(id+"F3.boolean.opBoolean","COPY",EDGE,{"derivedFrom":makeQuery(id+"F3.opExtrude","SWEPT_EDGE",EDGE,{"disambiguationData":[OSD([sQuery(id+"F0.wireOp",EDGE,"E0.top"),sQuery(id+"F2.wireOp",EDGE,"E2.5.0.0"),sQuery(id+"F2.wireOp",EDGE,"E2.5.0.3")])]})});
            var Q65;
            Q65=makeQuery(id+"F3.boolean.opBoolean","COPY",EDGE,{"derivedFrom":makeQuery(id+"F3.opExtrude","SWEPT_EDGE",EDGE,{"disambiguationData":[OSD([sQuery(id+"F0.wireOp",EDGE,"E0.top"),sQuery(id+"F2.wireOp",EDGE,"E2.6.0.0"),sQuery(id+"F2.wireOp",EDGE,"E2.6.0.3")])]})});
            var Q66;
            Q66=makeQuery(id+"F3.boolean.opBoolean","COPY",EDGE,{"derivedFrom":makeQuery(id+"F3.opExtrude","SWEPT_EDGE",EDGE,{"disambiguationData":[OSD([sQuery(id+"F0.wireOp",EDGE,"E0.top"),sQuery(id+"F2.wireOp",EDGE,"E2.7.0.0"),sQuery(id+"F2.wireOp",EDGE,"E2.7.0.3")])]})});
            var Q67;
            Q67=makeQuery(id+"F3.boolean.opBoolean","COPY",EDGE,{"derivedFrom":makeQuery(id+"F3.opExtrude","SWEPT_EDGE",EDGE,{"disambiguationData":[OSD([sQuery(id+"F0.wireOp",EDGE,"E0.top"),sQuery(id+"F2.wireOp",EDGE,"E2.8.0.0"),sQuery(id+"F2.wireOp",EDGE,"E2.8.0.3")])]})});
            var Q68;
            Q68=makeQuery(id+"F3.boolean.opBoolean","COPY",EDGE,{"derivedFrom":makeQuery(id+"F3.opExtrude","SWEPT_EDGE",EDGE,{"disambiguationData":[OSD([sQuery(id+"F0.wireOp",EDGE,"E0.top"),sQuery(id+"F2.wireOp",EDGE,"E15.MirrorCS"),sQuery(id+"F2.wireOp",EDGE,"E39.MirrorCS")])]})});
            var Q69;
            Q69=makeQuery(id+"F3.boolean.opBoolean","COPY",EDGE,{"derivedFrom":makeQuery(id+"F3.opExtrude","SWEPT_EDGE",EDGE,{"disambiguationData":[OSD([sQuery(id+"F0.wireOp",EDGE,"E0.top"),sQuery(id+"F2.wireOp",EDGE,"E11.MirrorCS"),sQuery(id+"F2.wireOp",EDGE,"E32.MirrorCS")])]})});
            var Q70;
            Q70=makeQuery(id+"F3.boolean.opBoolean","COPY",EDGE,{"derivedFrom":makeQuery(id+"F3.opExtrude","SWEPT_EDGE",EDGE,{"disambiguationData":[OSD([sQuery(id+"F0.wireOp",EDGE,"E0.top"),sQuery(id+"F2.wireOp",EDGE,"E20.MirrorCS"),sQuery(id+"F2.wireOp",EDGE,"E31.MirrorCS")])]})});
            var Q71;
            Q71=makeQuery(id+"F3.boolean.opBoolean","COPY",EDGE,{"derivedFrom":makeQuery(id+"F3.opExtrude","SWEPT_EDGE",EDGE,{"disambiguationData":[OSD([sQuery(id+"F0.wireOp",EDGE,"E0.top"),sQuery(id+"F2.wireOp",EDGE,"E9.MirrorCS"),sQuery(id+"F2.wireOp",EDGE,"E34.MirrorCS")])]})});
            var Q72;
            Q72=makeQuery(id+"F3.boolean.opBoolean","COPY",EDGE,{"derivedFrom":makeQuery(id+"F3.opExtrude","SWEPT_EDGE",EDGE,{"disambiguationData":[OSD([sQuery(id+"F0.wireOp",EDGE,"E0.top"),sQuery(id+"F2.wireOp",EDGE,"E14.MirrorCS"),sQuery(id+"F2.wireOp",EDGE,"E27.MirrorCS")])]})});
            var Q73;
            Q73=makeQuery(id+"F3.boolean.opBoolean","COPY",EDGE,{"derivedFrom":makeQuery(id+"F3.opExtrude","SWEPT_EDGE",EDGE,{"disambiguationData":[OSD([sQuery(id+"F0.wireOp",EDGE,"E0.top"),sQuery(id+"F2.wireOp",EDGE,"E18.MirrorCS"),sQuery(id+"F2.wireOp",EDGE,"E33.MirrorCS")])]})});
            var Q74;
            Q74=makeQuery(id+"F3.boolean.opBoolean","COPY",EDGE,{"derivedFrom":makeQuery(id+"F3.opExtrude","SWEPT_EDGE",EDGE,{"disambiguationData":[OSD([sQuery(id+"F0.wireOp",EDGE,"E0.top"),sQuery(id+"F2.wireOp",EDGE,"E5.MirrorCS"),sQuery(id+"F2.wireOp",EDGE,"E36.MirrorCS")])]})});
            var Q75;
            Q75=makeQuery(id+"F3.boolean.opBoolean","COPY",EDGE,{"derivedFrom":makeQuery(id+"F3.opExtrude","SWEPT_EDGE",EDGE,{"disambiguationData":[OSD([sQuery(id+"F0.wireOp",EDGE,"E0.top"),sQuery(id+"F2.wireOp",EDGE,"E12.MirrorCS"),sQuery(id+"F2.wireOp",EDGE,"E29.MirrorCS")])]})});
            var Q76;
            Q76=makeQuery(id+"F3.boolean.opBoolean","COPY",EDGE,{"derivedFrom":makeQuery(id+"F3.opExtrude","SWEPT_EDGE",EDGE,{"disambiguationData":[OSD([sQuery(id+"F0.wireOp",EDGE,"E0.top"),sQuery(id+"F2.wireOp",EDGE,"E19.MirrorCS"),sQuery(id+"F2.wireOp",EDGE,"E24.MirrorCS")])]})});
            fillet(context, id + "F4", {"entities" : qUnion([Q0, Q1, Q2, Q3, Q4, Q5, Q6, Q7, Q8, Q9, Q10, Q11, Q12, Q13, Q14, Q15, Q16, Q17, Q18, Q19, Q20, Q21, Q22, Q23, Q24, Q25, Q26, Q27, Q28, Q29, Q30, Q31, Q32, Q33, Q34, Q35, Q36, Q37, Q38, Q39, Q40, Q41, Q42, Q43, Q44, Q45, Q46, Q47, Q48, Q49, Q50, Q51, Q52, Q53, Q54, Q55, Q56, Q57, Q58, Q59, Q60, Q61, Q62, Q63, Q64, Q65, Q66, Q67, Q68, Q69, Q70, Q71, Q72, Q73, Q74, Q75, Q76]), "radius" : 0.5 * mm, "tangentPropagation" : true, "allowEdgeOverflow" : false});
        }
    });
